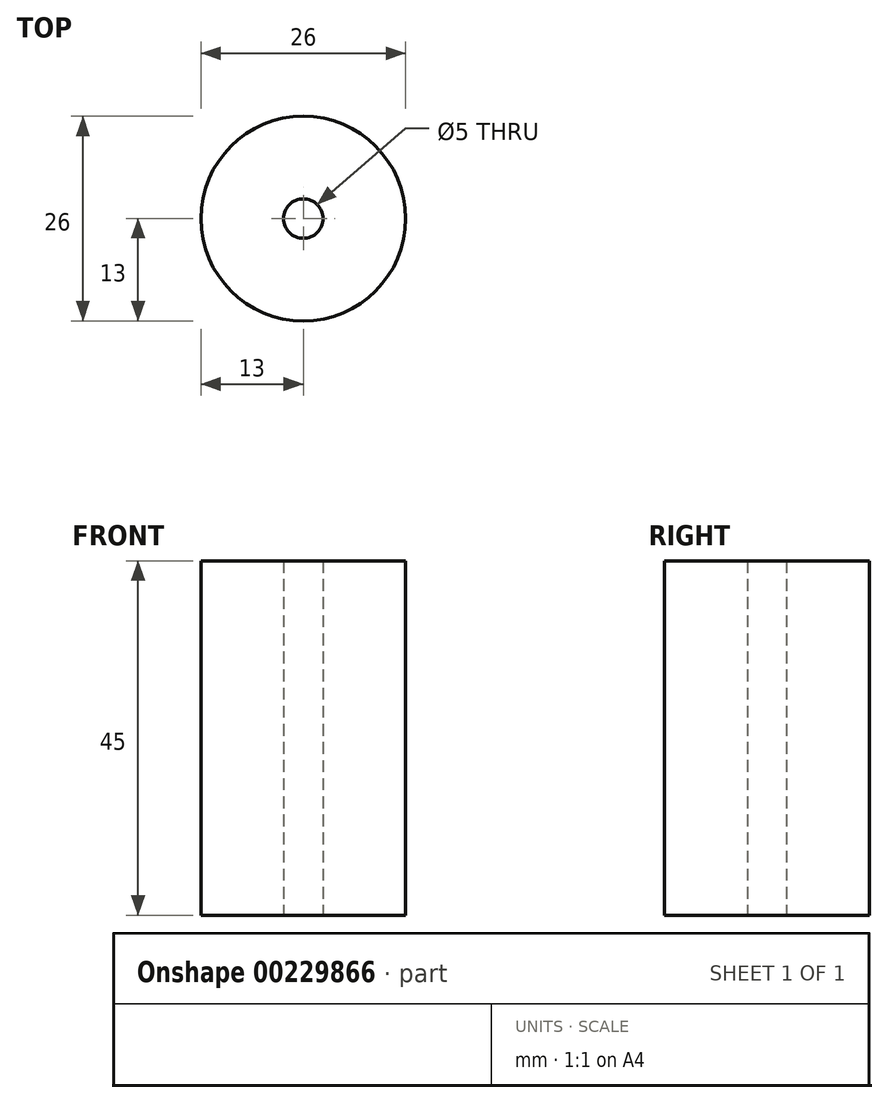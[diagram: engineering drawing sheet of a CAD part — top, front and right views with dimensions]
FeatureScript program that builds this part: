
annotation { "Feature Type Name" : "Feature", "Feature Type Description" : "" }
export const myFeature = defineFeature(function(context is Context, id is Id, definition is map)
    precondition{}
    {
        {
            var Q0;
            Q0=qCreatedBy(makeId("Top.planeOp"),FACE);
            var sketch = newSketch(context, id + "F0", { "sketchPlane" : qUnion([Q0])});
            skCircle(sketch, "E0", {"center": v(0, 0) * mm, "radius": 13 * mm});
            skCircle(sketch, "E1", {"center": v(0, 0) * mm, "radius": 2.5 * mm});
            skSolve(sketch);
        }
        {
            var Q0;
            Q0=makeQuery(id+"F0.imprint","IMPRINT",FACE,{"disambiguationData":[TD([[makeQuery(id+"F0.imprint","IMPRINT",EDGE,{"derivedFrom":sQuery(id+"F0.wireOp",EDGE,"E0")}),1.0]])]});
            extrude(context, id + "F1", {"entities" : qUnion([Q0]), "depth" : 45 * mm});
        }
    });
